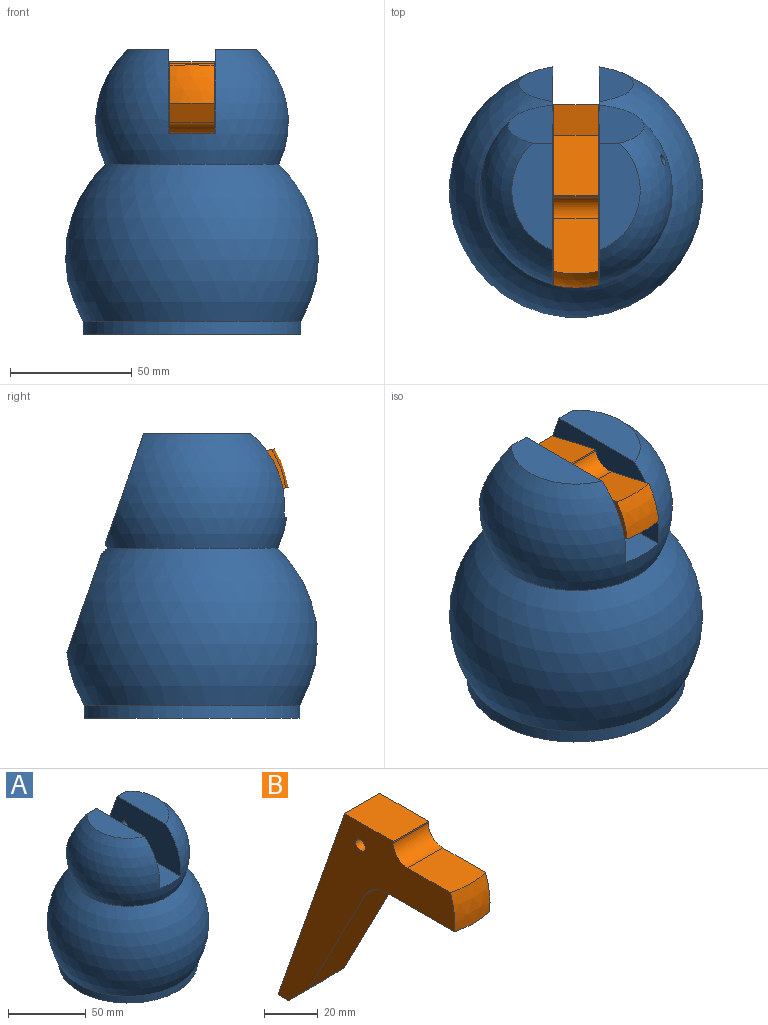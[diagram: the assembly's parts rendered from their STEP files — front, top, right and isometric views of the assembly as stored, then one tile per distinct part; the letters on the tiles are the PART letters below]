
ASSEMBLY  parts=2 mates=1
PART A: 17 faces, bbox 104.2x103.3x116.9 mm
  f0: cylinder r=44.77mm len=89.54mm, axis (0,0,-1), area 1398mm2, adj f1,f2,f6,f7
  f1: plane 89.54x88.51mm, normal (0,0,-1), area 5959.1mm2, adj f0,f6,f7,f8
  f2: sphere r=52.07mm, area 18816.3mm2, adj f0,f3,f6,f7,f10,f12
  f3: sphere r=39.69mm, area 8342.5mm2, adj f2,f4,f5,f6,f7,f9,f11,f13
  f4: plane 44.05x16.88mm, normal (0,0,1), area 578.3mm2, adj f3,f6,f13
  f5: plane 44.05x16.88mm, normal (0,0,1), area 578.3mm2, adj f3,f7,f11
  f6: plane 116.87x89.5mm, normal (1,0,0), area 4601.5mm2, adj f0,f1,f2,f3,f4,f8,f9,f12
  f7: plane 116.87x89.5mm, normal (-1,0,0), area 4601.5mm2, adj f0,f1,f2,f3,f5,f8,f9,f10
  f8: plane 82.55x28.94mm, normal (0,0.94,0.33), area 1666.4mm2, adj f1,f6,f7,f9
  f9: plane 37.21x19.05mm, normal (0,0,1), area 701.5mm2, adj f3,f6,f7,f8
  f10: plane 40.74x14.28mm, normal (0,0.94,0.33), area 437.5mm2, adj f2,f7
  f11: plane 45.17x18.47mm, normal (0,0.94,0.33), area 685.6mm2, adj f3,f5,f7
  f12: plane 40.74x14.28mm, normal (0,0.94,0.33), area 437.5mm2, adj f2,f6
  f13: plane 45.17x18.47mm, normal (0,0.94,0.33), area 685.6mm2, adj f3,f4,f6
  f14: cylinder r=2.29mm len=27.44mm, axis (1,0,0), area 378.9mm2, adj f3,f7
  f15: cylinder r=2.29mm len=13mm, axis (1,0,0), area 186.8mm2, adj f6,f16
  f16: plane 4.57x4.57mm, normal (1,0,0), area 16.4mm2, adj f15
PART B: 14 faces, bbox 19.6x93.8x99.7 mm
  f0: plane 18.42x5.42mm, normal (0,0,-1), area 99.8mm2, adj f1,f11,f12,f13
  f1: plane 99.7x34.95mm, normal (0,0.94,0.33), area 1945.4mm2, adj f0,f2,f11,f12
  f2: plane 25.4x18.42mm, normal (0,0,1), area 467.7mm2, adj f1,f3,f11,f12
  f3: plane 18.42x0.64mm, normal (0,-1,0), area 11.7mm2, adj f2,f4,f11,f12
  f4: cylinder r=7.62mm len=18.42mm, axis (-1,0,0), area 220.4mm2, adj f3,f5,f11,f12
  f5: plane 23.52x18.42mm, normal (0,0,1), area 425.7mm2, adj f4,f6,f11,f12
  f6: sphere r=38.16mm, area 314.7mm2, adj f5,f7,f11,f12
  f7: plane 36.78x18.42mm, normal (0,0,-1), area 670.4mm2, adj f6,f8,f11,f12
  f8: cylinder r=12.7mm len=18.42mm, axis (-1,0,0), area 255.9mm2, adj f7,f10,f11,f12
  f9: cylinder r=2.54mm len=18.42mm, axis (-1,0,0), area 293.9mm2, adj f11,f12
  f10: plane 56.65x29.26mm, normal (0,-0.89,-0.46), area 1174.1mm2, adj f8,f11,f12,f13
  f11: plane 99.7x92.68mm, normal (1,0,0), area 2491.4mm2, adj f0,f1,f2,f3,f4,f5,f6,f7
  f12: plane 99.7x92.68mm, normal (-1,0,0), area 2491.4mm2, adj f0,f1,f2,f3,f4,f5,f6,f7
  f13: plane 18.42x11.28mm, normal (0,-0.72,-0.7), area 289mm2, adj f0,f10,f11,f12
PLACE A at identity fixed
PLACE B rot(axis=(-1,0,0),12.4deg) t=(0,-20.87,4.97)mm
MATE revolute A.f14 <-> B.f9  axis (-1,0,0) through (0,12.42,98.43)mm
